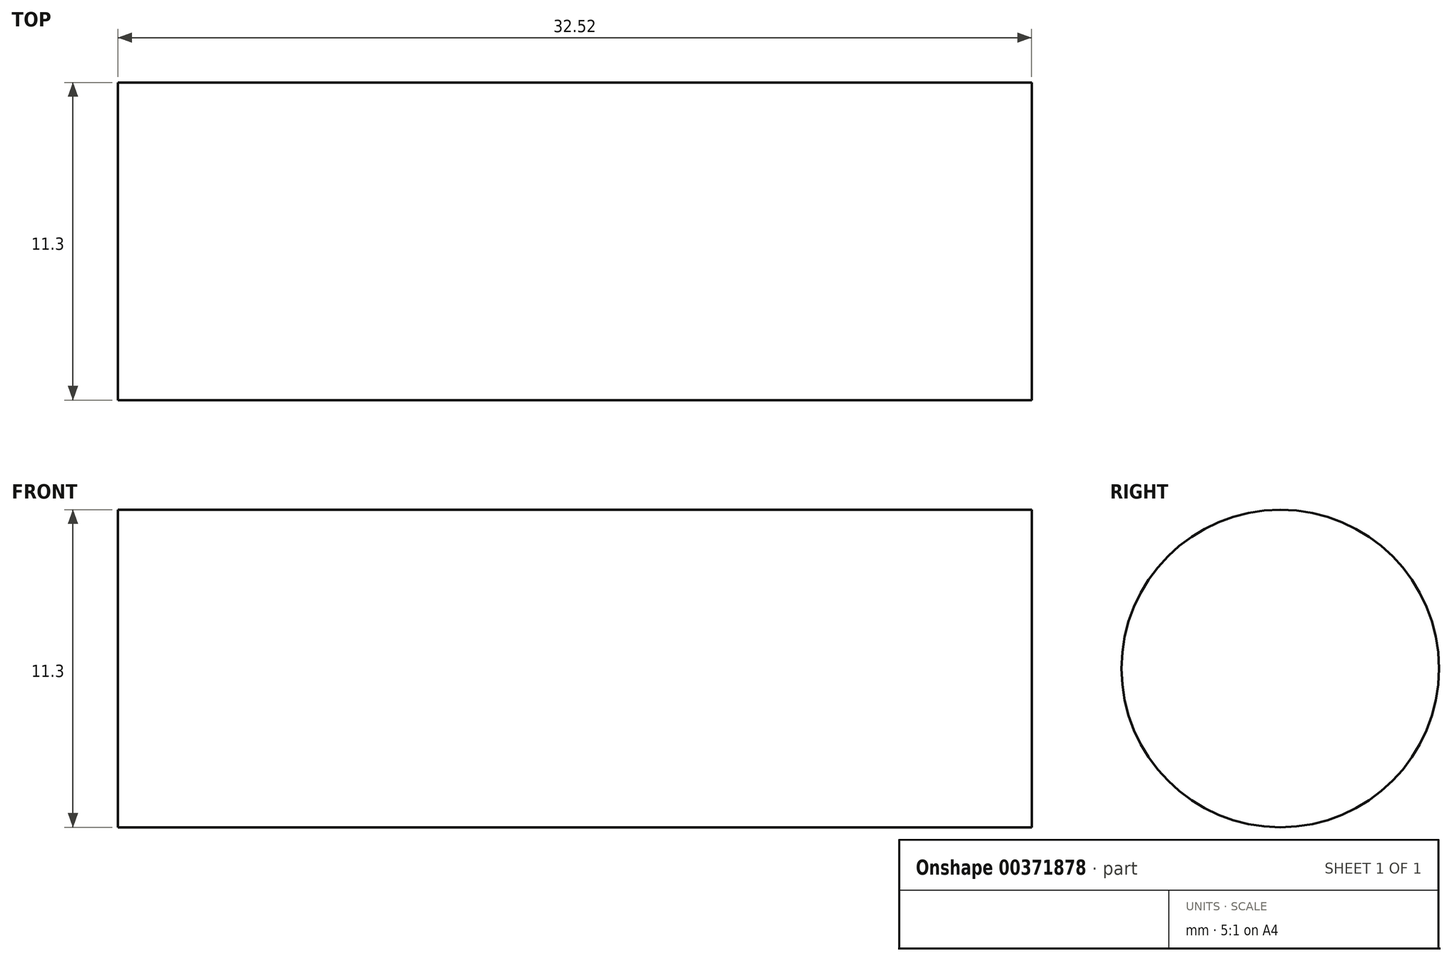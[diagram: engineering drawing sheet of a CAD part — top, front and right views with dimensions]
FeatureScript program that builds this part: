
annotation { "Feature Type Name" : "Feature", "Feature Type Description" : "" }
export const myFeature = defineFeature(function(context is Context, id is Id, definition is map)
    precondition{}
    {
        {
            var Q0;
            Q0=qCreatedBy(makeId("Top.planeOp"),FACE);
            var sketch = newSketch(context, id + "F0", { "sketchPlane" : qUnion([Q0])});
            skLineSegment(sketch, "E0.bottom", {"start": v(0, 0) * mm, "end": v(32.52, 0) * mm});
            skLineSegment(sketch, "E0.top", {"start": v(0, 5.65) * mm, "end": v(32.52, 5.65) * mm});
            skLineSegment(sketch, "E0.left", {"start": v(0, 0) * mm, "end": v(0, 5.65) * mm});
            skLineSegment(sketch, "E0.right", {"start": v(32.52, 0) * mm, "end": v(32.52, 5.65) * mm});
            skSolve(sketch);
        }
        {
            var Q0;
            Q0=makeQuery(id+"F0.imprint","IMPRINT",FACE,{"disambiguationData":[TD([[makeQuery(id+"F0.imprint","IMPRINT",EDGE,{"derivedFrom":sQuery(id+"F0.wireOp",EDGE,"E0.bottom")}),1.0]])]});
            var Q1;
            Q1=sQuery(id+"F0.wireOp",EDGE,"E0.bottom");
            revolve(context, id + "F1", {"surfaceOperationType" : NewSurfaceOperationType.NEW, "entities" : qUnion([Q0]), "axis" : qUnion([Q1]), "revolveType" : RevolveType.FULL});
        }
    });
